# Revit family: IEK_Держатель проводника круглого_8-10мм_Для жёлоба водостока
name_source: partatom
category: Обобщенные модели
units: mm (PartAtom-declared; Revit-internal decimal feet)

## family parameters
Может служить основой для арматурных стержней = Нет
Общий = Да
Основа = Грань
При загрузке вырезать с полостями = Нет
Размер круглого соединителя = Использовать диаметр
Тип детали = Нормальный
Точка расчета площади = Нет

## types (2) — shared parameters
ADSK_URL страницы изделия = https://www.iek.ru
ADSK_Версия Revit = 2019
ADSK_Версия семейства = 1.0
ADSK_Группирование = VIII. ЭЛЕМЕНТЫ ВНЕШНЕЙ МОЛНИЕЗАЩИТЫ
ADSK_Единица измерения = шт
ADSK_Завод-изготовитель = IEK
IEK_Описание = Держатель проводника круглого 8 – 10 мм для желоба водостока товарного знака IEK используется для закрепления прутка на желобе водостока. Пластины под фальц кровли прижимаются к основе держателя болтами М8.
zero-valued in all types: Отметка по умолчанию

## per-type parameters (varying)
| type | ADSK_Код изделия | ADSK_Масса | ADSK_Материал | ADSK_Материал наименование | ADSK_Наименование | IEK_URL | IEK_Цена за единицу | KSI_CMa_Строительные материалы |
| 8-10_Сталь оцинкованная | ZDP80-11-8-18 | 0.13 | Сталь оцинкованная | Сталь оцинкованная | Держатель проводника круглого 8-10мм для желоба водостока оцинкованная сталь IEK | https://www.iek.ru | 345 | 24.10.35.000.08.3.05.06-0001 |
| 8-10_Медь | ZDP80-50-8-18 | 0.15 | Медь | Медь | Держатель проводника круглого 8-10мм для желоба водостока медь IEK |  | 1352 | 10.2.01.02 |
